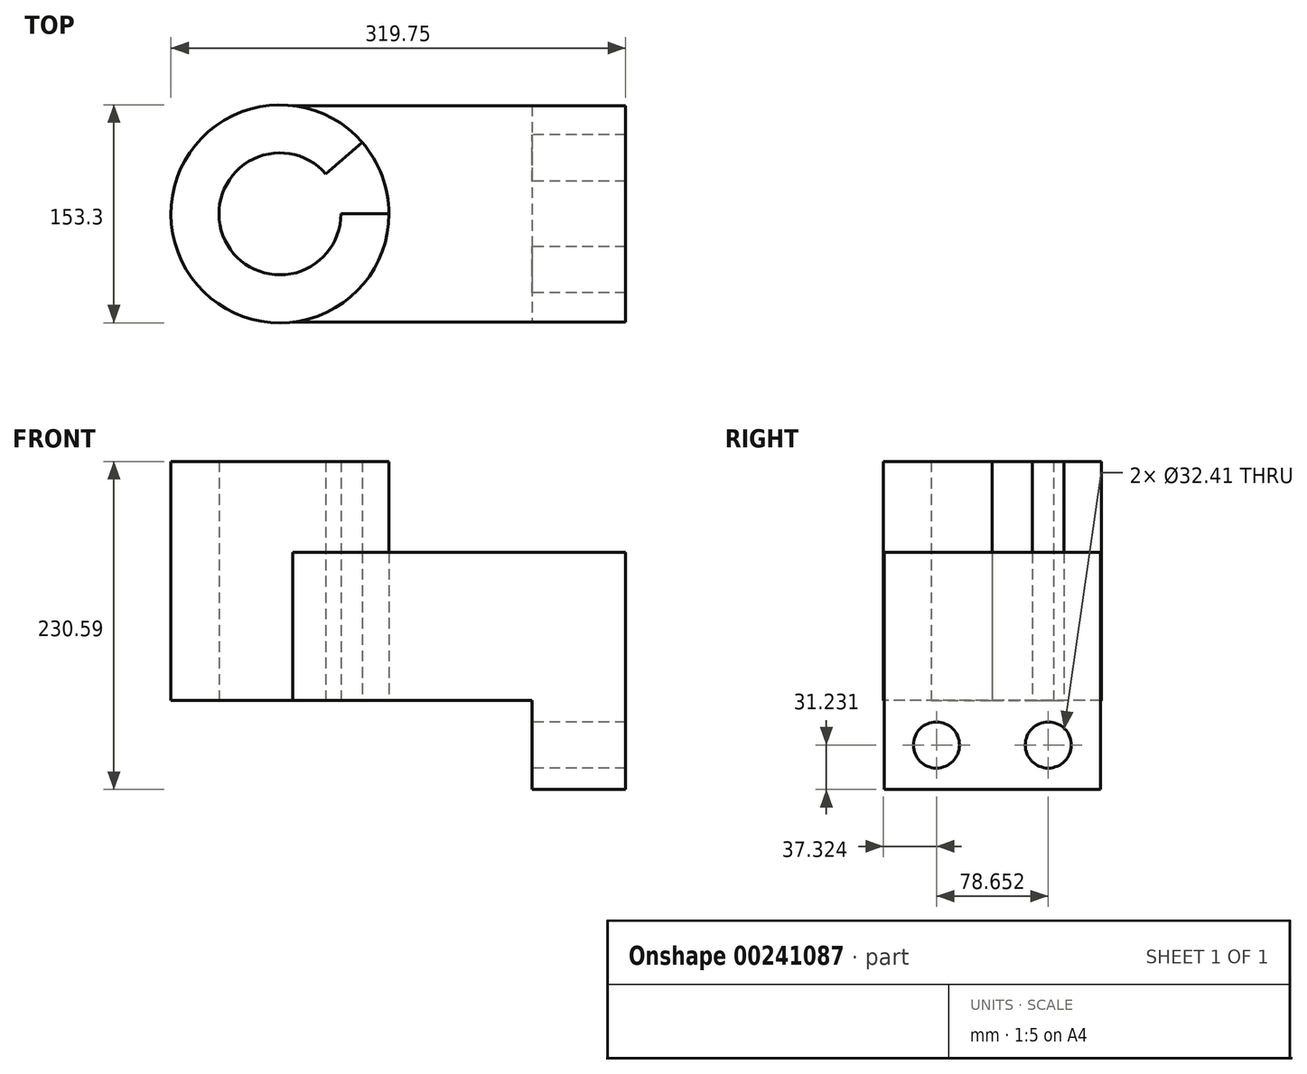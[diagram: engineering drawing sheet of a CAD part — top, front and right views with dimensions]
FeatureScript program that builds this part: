
annotation { "Feature Type Name" : "Feature", "Feature Type Description" : "" }
export const myFeature = defineFeature(function(context is Context, id is Id, definition is map)
    precondition{}
    {
        {
            var Q0;
            Q0=qCreatedBy(makeId("Top.planeOp"),FACE);
            var sketch = newSketch(context, id + "F0", { "sketchPlane" : qUnion([Q0])});
            skLineSegment(sketch, "E0.bottom", {"start": v(-76.65, 76.14) * mm, "end": v(100.66, 76.14) * mm});
            skLineSegment(sketch, "E0.top", {"start": v(-76.65, -76.14) * mm, "end": v(100.66, -76.14) * mm});
            skLineSegment(sketch, "E0.left", {"start": v(-76.65, 76.14) * mm, "end": v(-76.65, -76.14) * mm});
            skLineSegment(sketch, "E0.right", {"start": v(100.66, 76.14) * mm, "end": v(100.66, -76.14) * mm});
            skCircle(sketch, "E1", {"center": v(-76.65, 0) * mm, "radius": 76.65 * mm});
            skCircle(sketch, "E2", {"center": v(-76.65, 0) * mm, "radius": 42.89 * mm});
            skLineSegment(sketch, "E3", {"start": v(-76.65, 0) * mm, "end": v(-44.34, 28.2) * mm});
            skLineSegment(sketch, "E4", {"start": v(-44.34, 28.2) * mm, "end": v(-33.77, 0) * mm});
            skLineSegment(sketch, "E5", {"start": v(-76.65, 0) * mm, "end": v(-18.89, 50.4) * mm});
            skLineSegment(sketch, "E6", {"start": v(0, 0) * mm, "end": v(-18.89, 50.4) * mm});
            skLineSegment(sketch, "E7", {"start": v(0, 0) * mm, "end": v(-76.65, 0) * mm});
            skLineSegment(sketch, "E8", {"start": v(-76.65, 0) * mm, "end": v(-36.5, 15.05) * mm});
            skSolve(sketch);
        }
        {
            var Q0;
            Q0 = qSketchRegion(id + "F0", true);
            extrude(context, id + "F1", {"entities" : qUnion([Q0]), "depth" : 78.74 * mm});
        }
        {
            var Q0;
            {var subQ0=sQuery(id+"F0.wireOp",EDGE,"E0.left");var subQ5=sQuery(id+"F0.wireOp",EDGE,"E0.bottom");var subQ6=makeQuery(id+"F0.imprint","INTERSECT",VERTEX,{"derivedFrom":[subQ5,subQ0]});Q0=makeQuery(id+"F0.imprint","IMPRINT",FACE,{"disambiguationData":[TD([[makeQuery(id+"F0.imprint","IMPRINT",EDGE,{"disambiguationData":[TD([[subQ6,-1.0]])],"derivedFrom":subQ5}),1.0]])]});}
            var Q1;
            Q1=makeQuery(id+"F1.opExtrude","CAP_FACE",FACE,{"disambiguationData":[OSD([sQuery(id+"F0.wireOp",EDGE,"E0.bottom"),sQuery(id+"F0.wireOp",EDGE,"E0.top"),sQuery(id+"F0.wireOp",EDGE,"E0.right"),sQuery(id+"F0.wireOp",EDGE,"E1"),sQuery(id+"F0.wireOp",EDGE,"E2"),sQuery(id+"F0.wireOp",EDGE,"E5"),sQuery(id+"F0.wireOp",EDGE,"E7")])],"isStart":false});
            var Q2;
            Q2=makeQuery(id+"F1.opExtrude","CAP_FACE",FACE,{"disambiguationData":[OSD([sQuery(id+"F0.wireOp",EDGE,"E0.bottom"),sQuery(id+"F0.wireOp",EDGE,"E0.top"),sQuery(id+"F0.wireOp",EDGE,"E0.right"),sQuery(id+"F0.wireOp",EDGE,"E1"),sQuery(id+"F0.wireOp",EDGE,"E2"),sQuery(id+"F0.wireOp",EDGE,"E5"),sQuery(id+"F0.wireOp",EDGE,"E7")])],"isStart":true});
            extrude(context, id + "F2", {"entities" : qUnion([Q0, Q1, Q2]), "operationType" : NewBodyOperationType.ADD, "depth" : 25.4 * mm});
        }
        {
            var Q0;
            {var subQ3=sQuery(id+"F0.wireOp",EDGE,"E0.top");var subQ5=sQuery(id+"F0.wireOp",EDGE,"E0.left");var subQ6=makeQuery(id+"F0.imprint","INTERSECT",VERTEX,{"derivedFrom":[subQ3,subQ5]});Q0=makeQuery(id+"F0.imprint","IMPRINT",FACE,{"disambiguationData":[TD([[makeQuery(id+"F0.imprint","IMPRINT",EDGE,{"disambiguationData":[TD([[subQ6,-1.0]])],"derivedFrom":subQ3}),1.0]])]});}
            var Q1;
            {var subQ0=sQuery(id+"F0.wireOp",EDGE,"E0.left");var subQ5=sQuery(id+"F0.wireOp",EDGE,"E0.bottom");var subQ6=makeQuery(id+"F0.imprint","INTERSECT",VERTEX,{"derivedFrom":[subQ5,subQ0]});Q1=makeQuery(id+"F0.imprint","IMPRINT",FACE,{"disambiguationData":[TD([[makeQuery(id+"F0.imprint","IMPRINT",EDGE,{"disambiguationData":[TD([[subQ6,-1.0]])],"derivedFrom":subQ5}),1.0]])]});}
            var Q2;
            {var subQ3=sQuery(id+"F0.wireOp",EDGE,"E0.left");var subQ7=sQuery(id+"F0.wireOp",EDGE,"E0.bottom");var subQ9=makeQuery(id+"F0.imprint","INTERSECT",VERTEX,{"derivedFrom":[subQ7,subQ3]});Q2=makeQuery(id+"F0.imprint","IMPRINT",FACE,{"disambiguationData":[TD([[makeQuery(id+"F0.imprint","IMPRINT",EDGE,{"disambiguationData":[TD([[subQ9,-1.0]])],"derivedFrom":subQ7}),-1.0]])]});}
            extrude(context, id + "F3", {"entities" : qUnion([Q0, Q1, Q2]), "operationType" : NewBodyOperationType.ADD, "depth" : 168.15 * mm});
        }
        {
            var Q0;
            {var subQ0=sQuery(id+"F0.wireOp",EDGE,"E0.right");Q0=makeQuery(id+"F2.boolean.opBoolean","MERGE",FACE,{"derivedFrom":[makeQuery(id+"F1.opExtrude","SWEPT_FACE",FACE,{"disambiguationData":[OSD([subQ0])]}),makeQuery(id+"F2.opExtrude","SWEPT_FACE",FACE,{"disambiguationData":[OSD([subQ0]),TDD([makeQuery(id+"F1.opExtrude","CAP_EDGE",EDGE,{"disambiguationData":[OSD([subQ0])],"isStart":false})])]})]});}
            var sketch = newSketch(context, id + "F4", { "sketchPlane" : qUnion([Q0])});
            skLineSegment(sketch, "E9.bottom", {"start": v(-76.14, 104.14) * mm, "end": v(76.14, 104.14) * mm});
            skLineSegment(sketch, "E9.top", {"start": v(-76.14, -62.44) * mm, "end": v(76.14, -62.44) * mm});
            skLineSegment(sketch, "E9.left", {"start": v(-76.14, 104.14) * mm, "end": v(-76.14, -62.44) * mm});
            skLineSegment(sketch, "E9.right", {"start": v(76.14, 104.14) * mm, "end": v(76.14, -62.44) * mm});
            skCircle(sketch, "E10", {"center": v(-39.33, -31.2) * mm, "radius": 16.2 * mm});
            skCircle(sketch, "E11.MirrorC", {"center": v(39.33, -31.2) * mm, "radius": 16.2 * mm});
            skSolve(sketch);
        }
        {
            var Q0;
            Q0 = qSketchRegion(id + "F4", true);
            extrude(context, id + "F5", {"entities" : qUnion([Q0]), "operationType" : NewBodyOperationType.ADD, "depth" : 65.8 * mm});
        }
    });
